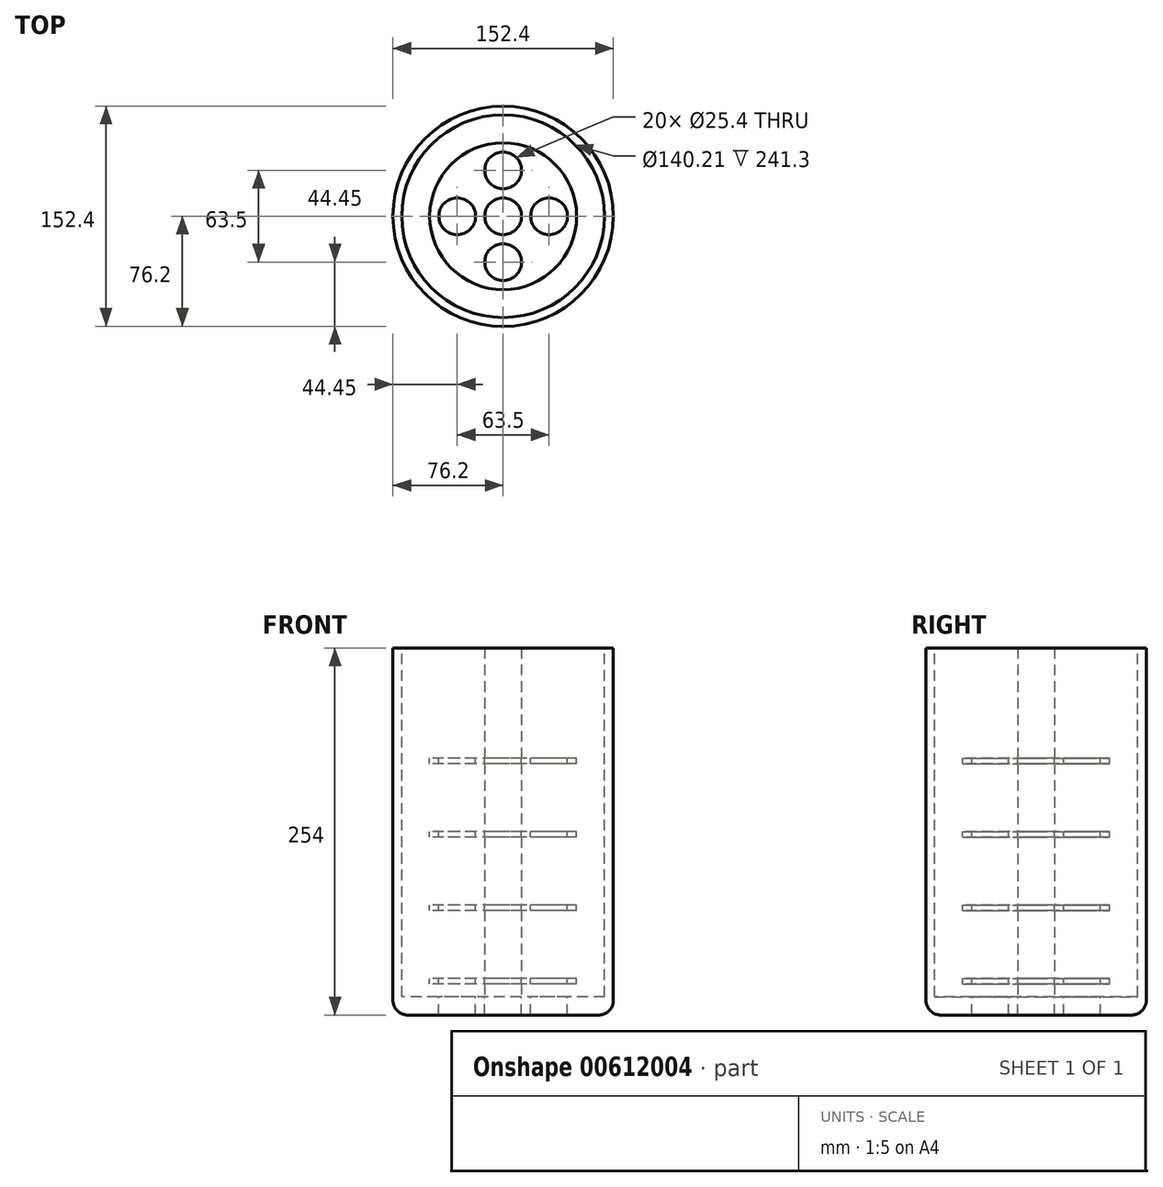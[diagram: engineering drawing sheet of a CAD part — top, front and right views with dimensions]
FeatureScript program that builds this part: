
annotation { "Feature Type Name" : "Feature", "Feature Type Description" : "" }
export const myFeature = defineFeature(function(context is Context, id is Id, definition is map)
    precondition{}
    {
        {
            var Q0;
            Q0=qCreatedBy(makeId("Top.planeOp"),FACE);
            var sketch = newSketch(context, id + "F0", { "sketchPlane" : qUnion([Q0])});
            skCircle(sketch, "E0", {"center": v(0, 0) * mm, "radius": 76.2 * mm});
            skSolve(sketch);
        }
        {
            var Q0;
            Q0 = qSketchRegion(id + "F0", true);
            extrude(context, id + "F1", {"entities" : qUnion([Q0]), "endBound" : BoundingType.SYMMETRIC, "depth" : 254 * mm, "offsetDistance" : 25.4 * mm});
        }
        {
            var Q0;
            Q0=makeQuery(id+"F1.opExtrude","CAP_FACE",FACE,{"disambiguationData":[OSD([sQuery(id+"F0.wireOp",EDGE,"E0")])],"isStart":false});
            var sketch = newSketch(context, id + "F2", { "sketchPlane" : qUnion([Q0])});
            skCircle(sketch, "E1.0", {"center": v(0, 0) * mm, "radius": 70.1 * mm});
            skSolve(sketch);
        }
        {
            var Q0;
            Q0 = qSketchRegion(id + "F2", true);
            extrude(context, id + "F3", {"entities" : qUnion([Q0]), "operationType" : NewBodyOperationType.REMOVE, "oppositeDirection" : true, "depth" : 241.3 * mm, "offsetDistance" : 25.4 * mm});
        }
        {
            var Q0;
            Q0=makeQuery(id+"F3.boolean.opBoolean","COPY",FACE,{"derivedFrom":makeQuery(id+"F3.opExtrude","CAP_FACE",FACE,{"disambiguationData":[OSD([sQuery(id+"F2.wireOp",EDGE,"E1.0")])],"isStart":false})});
            var sketch = newSketch(context, id + "F4", { "sketchPlane" : qUnion([Q0])});
            skCircle(sketch, "E2", {"center": v(0, 0) * mm, "radius": 12.7 * mm});
            skSolve(sketch);
        }
        {
            var Q0;
            Q0=makeQuery(id+"F4.imprint","IMPRINT",FACE,{"disambiguationData":[TD([[makeQuery(id+"F4.imprint","IMPRINT",EDGE,{"derivedFrom":sQuery(id+"F4.wireOp",EDGE,"E2")}),1.0]])]});
            extrude(context, id + "F5", {"entities" : qUnion([Q0]), "depth" : 241.3 * mm, "offsetDistance" : 25.4 * mm});
        }
        {
            var Q0;
            Q0=makeQuery(id+"F1.opExtrude","CAP_EDGE",EDGE,{"disambiguationData":[OSD([sQuery(id+"F0.wireOp",EDGE,"E0")])],"isStart":true});
            fillet(context, id + "F6", {"entities" : qUnion([Q0]), "radius" : 10.16 * mm, "tangentPropagation" : true, "allowEdgeOverflow" : false});
        }
        {
            var Q0;
            Q0=qCreatedBy(makeId("Front.planeOp"),FACE);
            var sketch = newSketch(context, id + "F7", { "sketchPlane" : qUnion([Q0])});
            skLineSegment(sketch, "E3.bottom", {"start": v(0, 50.8) * mm, "end": v(-50.8, 50.8) * mm});
            skLineSegment(sketch, "E3.top", {"start": v(0, 46.99) * mm, "end": v(-50.8, 46.99) * mm});
            skLineSegment(sketch, "E3.right", {"start": v(-50.8, 46.99) * mm, "end": v(-50.8, 50.8) * mm});
            skLineSegment(sketch, "E4.bottom", {"start": v(0, 0) * mm, "end": v(-50.8, 0) * mm});
            skLineSegment(sketch, "E4.top", {"start": v(0, -3.8) * mm, "end": v(-50.8, -3.8) * mm});
            skLineSegment(sketch, "E4.right", {"start": v(-50.8, -3.81) * mm, "end": v(-50.8, 0) * mm});
            skPoint(sketch, "E4.middle", {"position": v(0, 0) * mm});
            skLineSegment(sketch, "E5.bottom", {"start": v(0, -50.8) * mm, "end": v(-50.8, -50.8) * mm});
            skLineSegment(sketch, "E5.top", {"start": v(0, -54.6) * mm, "end": v(-50.8, -54.6) * mm});
            skLineSegment(sketch, "E5.right", {"start": v(-50.8, -54.6) * mm, "end": v(-50.8, -50.8) * mm});
            skLineSegment(sketch, "E6.bottom", {"start": v(0, -101.6) * mm, "end": v(-50.8, -101.6) * mm});
            skLineSegment(sketch, "E6.top", {"start": v(0, -105.4) * mm, "end": v(-50.8, -105.4) * mm});
            skLineSegment(sketch, "E6.right", {"start": v(-50.8, -105.4) * mm, "end": v(-50.8, -101.6) * mm});
            skLineSegment(sketch, "E7", {"start": v(0, 50.8) * mm, "end": v(0, 46.99) * mm});
            skLineSegment(sketch, "E8", {"start": v(0, 0) * mm, "end": v(0, -3.8) * mm});
            skLineSegment(sketch, "E9", {"start": v(0, -105.4) * mm, "end": v(0, -101.6) * mm});
            skLineSegment(sketch, "E10", {"start": v(0, -54.6) * mm, "end": v(0, -50.8) * mm});
            skLineSegment(sketch, "E11", {"start": v(0, 46.99) * mm, "end": v(0, -3.8) * mm, "construction": true});
            skLineSegment(sketch, "E12", {"start": v(0, -54.6) * mm, "end": v(0, -3.8) * mm, "construction": true});
            skLineSegment(sketch, "E13", {"start": v(0, -105.4) * mm, "end": v(0, -54.6) * mm, "construction": true});
            skSolve(sketch);
        }
        {
            var Q0;
            Q0 = qSketchRegion(id + "F7", true);
            var Q1;
            Q1=sQuery(id+"F7.wireOp",EDGE,"E11");
            revolve(context, id + "F8", {"operationType" : NewBodyOperationType.ADD, "entities" : qUnion([Q0]), "axis" : qUnion([Q1]), "revolveType" : RevolveType.FULL});
        }
        {
            var Q0;
            Q0=makeQuery(id+"F8.opRevolve","SWEPT_FACE",FACE,{"disambiguationData":[OSD([sQuery(id+"F7.wireOp",EDGE,"E3.bottom")])]});
            var sketch = newSketch(context, id + "F9", { "sketchPlane" : qUnion([Q0])});
            skCircle(sketch, "E14", {"center": v(0, 31.75) * mm, "radius": 12.7 * mm});
            skLineSegment(sketch, "E15", {"start": v(0, 12.7) * mm, "end": v(0, 31.75) * mm, "construction": true});
            skLineSegment(sketch, "E16", {"start": v(0, 50.8) * mm, "end": v(0, 31.75) * mm, "construction": true});
            skCircle(sketch, "E17.1.0", {"center": v(-31.75, 0) * mm, "radius": 12.7 * mm});
            skCircle(sketch, "E17.2.0", {"center": v(0, -31.75) * mm, "radius": 12.7 * mm});
            skCircle(sketch, "E17.3.0", {"center": v(31.75, 0) * mm, "radius": 12.7 * mm});
            skPoint(sketch, "E17.center", {"position": v(0, 0) * mm});
            skSolve(sketch);
        }
        {
            var Q0;
            Q0 = qSketchRegion(id + "F9", true);
            extrude(context, id + "F10", {"entities" : qUnion([Q0]), "operationType" : NewBodyOperationType.REMOVE, "endBound" : BoundingType.THROUGH_ALL, "oppositeDirection" : true, "depth" : 25.4 * mm, "offsetDistance" : 25.4 * mm});
        }
    });
